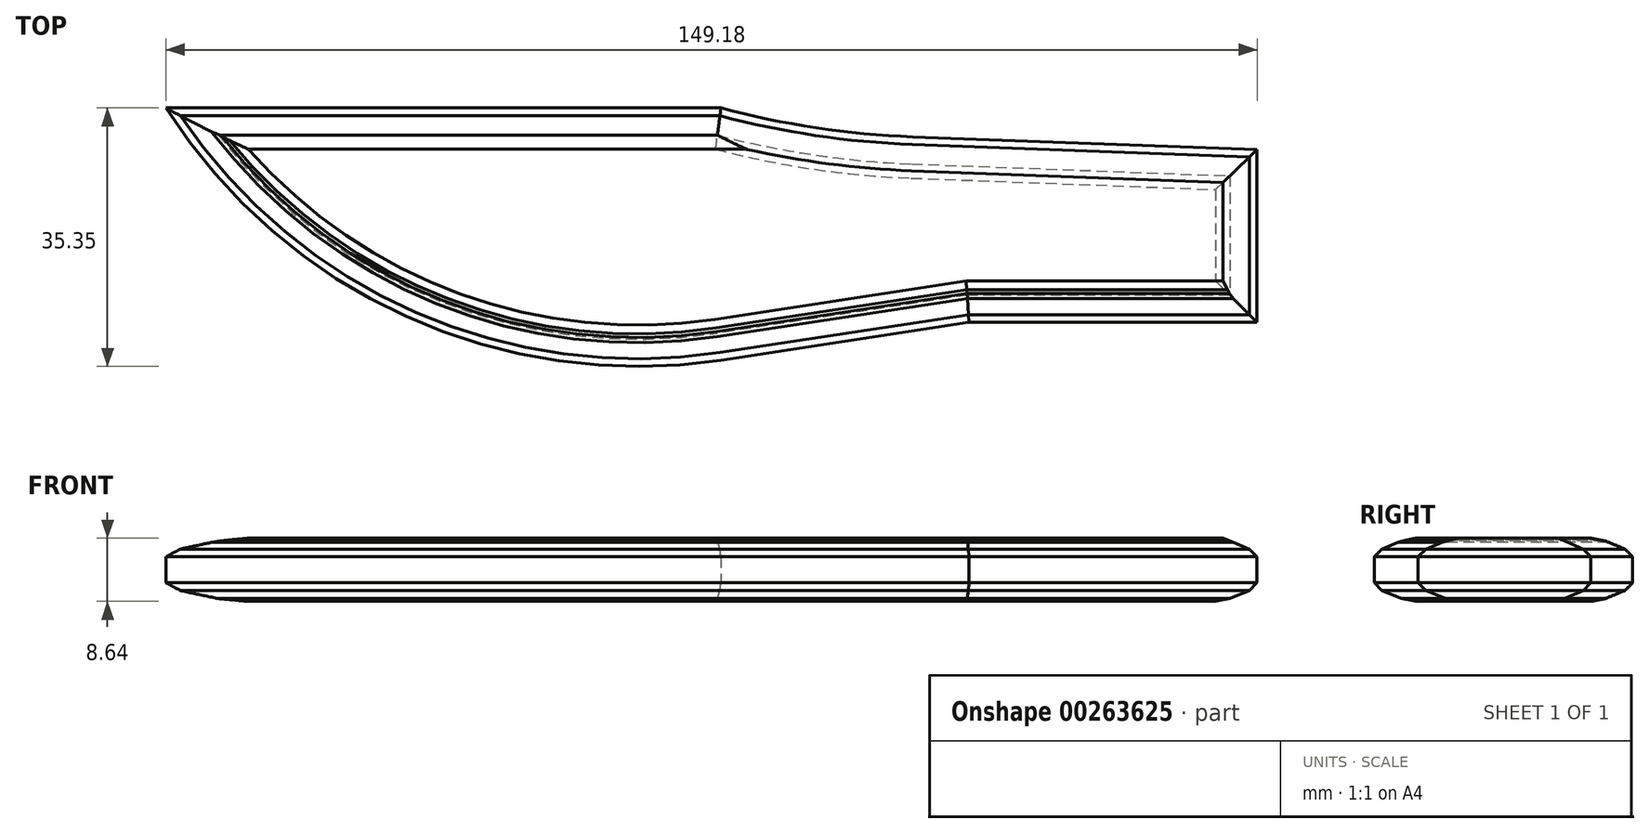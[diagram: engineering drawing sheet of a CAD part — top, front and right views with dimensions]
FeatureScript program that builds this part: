
annotation { "Feature Type Name" : "Feature", "Feature Type Description" : "" }
export const myFeature = defineFeature(function(context is Context, id is Id, definition is map)
    precondition{}
    {
        {
            var Q0;
            Q0=qCreatedBy(makeId("Top.planeOp"),FACE);
            var sketch = newSketch(context, id + "F0", { "sketchPlane" : qUnion([Q0])});
            skLineSegment(sketch, "E0", {"start": v(-62.27, 14.58) * mm, "end": v(13.6, 14.58) * mm});
            skArc(sketch, "E1", {"start": v(-62.27, 14.58) * mm, "mid": v(-29.46, -13.93) * mm, "end": v(13.6, -19.9) * mm});
            skLineSegment(sketch, "E2", {"start": v(13.6, -19.9) * mm, "end": v(47.54, -14.74) * mm});
            skLineSegment(sketch, "E3", {"start": v(47.54, -14.74) * mm, "end": v(86.9, -14.74) * mm});
            skLineSegment(sketch, "E4", {"start": v(86.9, -14.74) * mm, "end": v(86.9, 8.87) * mm});
            skLineSegment(sketch, "E5", {"start": v(86.9, 8.87) * mm, "end": v(39.8, 10.64) * mm});
            skArc(sketch, "E6", {"start": v(13.6, 14.58) * mm, "mid": v(26.6, 11.88) * mm, "end": v(39.8, 10.64) * mm});
            skSolve(sketch);
        }
        {
            var Q0;
            Q0 = qSketchRegion(id + "F0", true);
            extrude(context, id + "F1", {"entities" : qUnion([Q0]), "depth" : 8.64 * mm});
        }
        {
            var Q0;
            Q0=makeQuery(id+"F1.opExtrude","CAP_FACE",FACE,{"disambiguationData":[OSD([sQuery(id+"F0.wireOp",EDGE,"E0"),sQuery(id+"F0.wireOp",EDGE,"E1"),sQuery(id+"F0.wireOp",EDGE,"E2"),sQuery(id+"F0.wireOp",EDGE,"E3"),sQuery(id+"F0.wireOp",EDGE,"E4"),sQuery(id+"F0.wireOp",EDGE,"E5"),sQuery(id+"F0.wireOp",EDGE,"E6")])],"isStart":true});
            var Q1;
            Q1=makeQuery(id+"F1.opExtrude","CAP_FACE",FACE,{"disambiguationData":[OSD([sQuery(id+"F0.wireOp",EDGE,"E0"),sQuery(id+"F0.wireOp",EDGE,"E1"),sQuery(id+"F0.wireOp",EDGE,"E2"),sQuery(id+"F0.wireOp",EDGE,"E3"),sQuery(id+"F0.wireOp",EDGE,"E4"),sQuery(id+"F0.wireOp",EDGE,"E5"),sQuery(id+"F0.wireOp",EDGE,"E6")])],"isStart":false});
            chamfer(context, id + "F2", {"entities" : qUnion([Q0, Q1]), "width" : 2.54 * mm, "tangentPropagation" : true});
        }
        {
            var Q0;
            Q0=makeQuery(id+"F1.opExtrude","CAP_FACE",FACE,{"disambiguationData":[OSD([sQuery(id+"F0.wireOp",EDGE,"E0"),sQuery(id+"F0.wireOp",EDGE,"E1"),sQuery(id+"F0.wireOp",EDGE,"E2"),sQuery(id+"F0.wireOp",EDGE,"E3"),sQuery(id+"F0.wireOp",EDGE,"E4"),sQuery(id+"F0.wireOp",EDGE,"E5"),sQuery(id+"F0.wireOp",EDGE,"E6")])],"isStart":true});
            var Q1;
            Q1=makeQuery(id+"F1.opExtrude","CAP_FACE",FACE,{"disambiguationData":[OSD([sQuery(id+"F0.wireOp",EDGE,"E0"),sQuery(id+"F0.wireOp",EDGE,"E1"),sQuery(id+"F0.wireOp",EDGE,"E2"),sQuery(id+"F0.wireOp",EDGE,"E3"),sQuery(id+"F0.wireOp",EDGE,"E4"),sQuery(id+"F0.wireOp",EDGE,"E5"),sQuery(id+"F0.wireOp",EDGE,"E6")])],"isStart":false});
            chamfer(context, id + "F3", {"entities" : qUnion([Q0, Q1]), "width" : 5.08 * mm, "tangentPropagation" : true});
        }
        {
            var Q0;
            Q0=makeQuery(id+"F1.opExtrude","CAP_FACE",FACE,{"disambiguationData":[OSD([sQuery(id+"F0.wireOp",EDGE,"E0"),sQuery(id+"F0.wireOp",EDGE,"E1"),sQuery(id+"F0.wireOp",EDGE,"E2"),sQuery(id+"F0.wireOp",EDGE,"E3"),sQuery(id+"F0.wireOp",EDGE,"E4"),sQuery(id+"F0.wireOp",EDGE,"E5"),sQuery(id+"F0.wireOp",EDGE,"E6")])],"isStart":true});
            chamfer(context, id + "F4", {"entities" : qUnion([Q0]), "width" : 5.08 * mm, "tangentPropagation" : true});
        }
        {
            var Q0;
            {var subQ0=sQuery(id+"F0.wireOp",EDGE,"E1");var subQ1=makeQuery(id+"F1.opExtrude","CAP_FACE",FACE,{"disambiguationData":[OSD([sQuery(id+"F0.wireOp",EDGE,"E0"),subQ0,sQuery(id+"F0.wireOp",EDGE,"E2"),sQuery(id+"F0.wireOp",EDGE,"E3"),sQuery(id+"F0.wireOp",EDGE,"E4"),sQuery(id+"F0.wireOp",EDGE,"E5"),sQuery(id+"F0.wireOp",EDGE,"E6")])],"isStart":true});Q0=makeQuery(id+"F3.opChamfer","BLEND_EDGE",EDGE,{"blendedFrom":[makeQuery(id+"F2.opChamfer","BLEND_EDGE",EDGE,{"blendedFrom":[makeQuery(id+"F1.opExtrude","CAP_EDGE",EDGE,{"disambiguationData":[OSD([subQ0])],"isStart":true}),subQ1],"blendedInto":[subQ1]}),subQ1],"blendedInto":[subQ1]});}
            var Q1;
            {var subQ0=sQuery(id+"F0.wireOp",EDGE,"E1");var subQ1=makeQuery(id+"F1.opExtrude","CAP_FACE",FACE,{"disambiguationData":[OSD([sQuery(id+"F0.wireOp",EDGE,"E0"),subQ0,sQuery(id+"F0.wireOp",EDGE,"E2"),sQuery(id+"F0.wireOp",EDGE,"E3"),sQuery(id+"F0.wireOp",EDGE,"E4"),sQuery(id+"F0.wireOp",EDGE,"E5"),sQuery(id+"F0.wireOp",EDGE,"E6")])],"isStart":false});Q1=makeQuery(id+"F3.opChamfer","BLEND_EDGE",EDGE,{"blendedFrom":[makeQuery(id+"F2.opChamfer","BLEND_EDGE",EDGE,{"blendedFrom":[makeQuery(id+"F1.opExtrude","CAP_EDGE",EDGE,{"disambiguationData":[OSD([subQ0])],"isStart":false}),subQ1],"blendedInto":[subQ1]}),subQ1],"blendedInto":[subQ1]});}
            var Q2;
            {var subQ0=sQuery(id+"F0.wireOp",EDGE,"E0");var subQ1=makeQuery(id+"F1.opExtrude","CAP_FACE",FACE,{"disambiguationData":[OSD([subQ0,sQuery(id+"F0.wireOp",EDGE,"E1"),sQuery(id+"F0.wireOp",EDGE,"E2"),sQuery(id+"F0.wireOp",EDGE,"E3"),sQuery(id+"F0.wireOp",EDGE,"E4"),sQuery(id+"F0.wireOp",EDGE,"E5"),sQuery(id+"F0.wireOp",EDGE,"E6")])],"isStart":true});Q2=makeQuery(id+"F3.opChamfer","BLEND_EDGE",EDGE,{"blendedFrom":[makeQuery(id+"F2.opChamfer","BLEND_EDGE",EDGE,{"blendedFrom":[makeQuery(id+"F1.opExtrude","CAP_EDGE",EDGE,{"disambiguationData":[OSD([subQ0])],"isStart":true}),subQ1],"blendedInto":[subQ1]}),subQ1],"blendedInto":[subQ1]});}
            var Q3;
            {var subQ0=sQuery(id+"F0.wireOp",EDGE,"E0");var subQ1=makeQuery(id+"F1.opExtrude","CAP_FACE",FACE,{"disambiguationData":[OSD([subQ0,sQuery(id+"F0.wireOp",EDGE,"E1"),sQuery(id+"F0.wireOp",EDGE,"E2"),sQuery(id+"F0.wireOp",EDGE,"E3"),sQuery(id+"F0.wireOp",EDGE,"E4"),sQuery(id+"F0.wireOp",EDGE,"E5"),sQuery(id+"F0.wireOp",EDGE,"E6")])],"isStart":false});Q3=makeQuery(id+"F3.opChamfer","BLEND_EDGE",EDGE,{"blendedFrom":[makeQuery(id+"F2.opChamfer","BLEND_EDGE",EDGE,{"blendedFrom":[makeQuery(id+"F1.opExtrude","CAP_EDGE",EDGE,{"disambiguationData":[OSD([subQ0])],"isStart":false}),subQ1],"blendedInto":[subQ1]}),subQ1],"blendedInto":[subQ1]});}
            chamfer(context, id + "F5", {"entities" : qUnion([Q0, Q1, Q2, Q3]), "width" : 5.08 * mm, "tangentPropagation" : true});
        }
        {
            var Q0;
            {var subQ0=sQuery(id+"F0.wireOp",EDGE,"E6");var subQ1=sQuery(id+"F0.wireOp",EDGE,"E5");var subQ2=sQuery(id+"F0.wireOp",EDGE,"E4");var subQ3=sQuery(id+"F0.wireOp",EDGE,"E3");var subQ4=sQuery(id+"F0.wireOp",EDGE,"E2");var subQ5=sQuery(id+"F0.wireOp",EDGE,"E1");var subQ6=sQuery(id+"F0.wireOp",EDGE,"E0");var subQ7=makeQuery(id+"F1.opExtrude","CAP_FACE",FACE,{"disambiguationData":[OSD([subQ6,subQ5,subQ4,subQ3,subQ2,subQ1,subQ0])],"isStart":true});var subQ8=makeQuery(id+"F2.opChamfer","BLEND_EDGE",EDGE,{"blendedFrom":[makeQuery(id+"F1.opExtrude","CAP_EDGE",EDGE,{"disambiguationData":[OSD([subQ5])],"isStart":true}),subQ7],"blendedInto":[subQ7]});Q0=makeQuery(id+"F5.opChamfer","BLEND_EDGE",EDGE,{"blendedFrom":[makeQuery(id+"F3.opChamfer","BLEND_EDGE",EDGE,{"blendedFrom":[subQ8,subQ7],"blendedInto":[subQ7]}),makeQuery(id+"F3.opChamfer","BLEND_FACE",FACE,{"disambiguationData":[OSD([subQ6,subQ5,subQ4,subQ3,subQ2,subQ1,subQ0]),TDD([subQ8])]})],"blendedInto":[makeQuery(id+"F3.opChamfer","BLEND_FACE",FACE,{"disambiguationData":[OSD([subQ6,subQ5,subQ4,subQ3,subQ2,subQ1,subQ0]),TDD([subQ8])]})]});}
            var Q1;
            {var subQ0=sQuery(id+"F0.wireOp",EDGE,"E6");var subQ1=sQuery(id+"F0.wireOp",EDGE,"E5");var subQ2=sQuery(id+"F0.wireOp",EDGE,"E4");var subQ3=sQuery(id+"F0.wireOp",EDGE,"E3");var subQ4=sQuery(id+"F0.wireOp",EDGE,"E2");var subQ5=sQuery(id+"F0.wireOp",EDGE,"E1");var subQ6=sQuery(id+"F0.wireOp",EDGE,"E0");var subQ7=makeQuery(id+"F1.opExtrude","CAP_FACE",FACE,{"disambiguationData":[OSD([subQ6,subQ5,subQ4,subQ3,subQ2,subQ1,subQ0])],"isStart":false});var subQ8=makeQuery(id+"F2.opChamfer","BLEND_EDGE",EDGE,{"blendedFrom":[makeQuery(id+"F1.opExtrude","CAP_EDGE",EDGE,{"disambiguationData":[OSD([subQ5])],"isStart":false}),subQ7],"blendedInto":[subQ7]});Q1=makeQuery(id+"F5.opChamfer","BLEND_EDGE",EDGE,{"blendedFrom":[makeQuery(id+"F3.opChamfer","BLEND_EDGE",EDGE,{"blendedFrom":[subQ8,subQ7],"blendedInto":[subQ7]}),makeQuery(id+"F3.opChamfer","BLEND_FACE",FACE,{"disambiguationData":[OSD([subQ6,subQ5,subQ4,subQ3,subQ2,subQ1,subQ0]),TDD([subQ8])]})],"blendedInto":[makeQuery(id+"F3.opChamfer","BLEND_FACE",FACE,{"disambiguationData":[OSD([subQ6,subQ5,subQ4,subQ3,subQ2,subQ1,subQ0]),TDD([subQ8])]})]});}
            chamfer(context, id + "F6", {"entities" : qUnion([Q0, Q1]), "width" : 5.08 * mm, "tangentPropagation" : true});
        }
        {
            var Q0;
            {var subQ0=sQuery(id+"F0.wireOp",EDGE,"E6");var subQ1=sQuery(id+"F0.wireOp",EDGE,"E5");var subQ2=sQuery(id+"F0.wireOp",EDGE,"E4");var subQ3=sQuery(id+"F0.wireOp",EDGE,"E3");var subQ4=sQuery(id+"F0.wireOp",EDGE,"E2");var subQ5=sQuery(id+"F0.wireOp",EDGE,"E1");var subQ6=sQuery(id+"F0.wireOp",EDGE,"E0");var subQ7=makeQuery(id+"F1.opExtrude","CAP_FACE",FACE,{"disambiguationData":[OSD([subQ6,subQ5,subQ4,subQ3,subQ2,subQ1,subQ0])],"isStart":true});var subQ8=makeQuery(id+"F2.opChamfer","BLEND_EDGE",EDGE,{"blendedFrom":[makeQuery(id+"F1.opExtrude","CAP_EDGE",EDGE,{"disambiguationData":[OSD([subQ4])],"isStart":true}),subQ7],"blendedInto":[subQ7]});var subQ9=makeQuery(id+"F3.opChamfer","BLEND_EDGE",EDGE,{"blendedFrom":[subQ8,subQ7],"blendedInto":[subQ7]});Q0=makeQuery(id+"F6.opChamfer","BLEND_EDGE",EDGE,{"blendedFrom":[makeQuery(id+"F5.opChamfer","BLEND_EDGE",EDGE,{"blendedFrom":[subQ9,makeQuery(id+"F3.opChamfer","BLEND_FACE",FACE,{"disambiguationData":[OSD([subQ6,subQ5,subQ4,subQ3,subQ2,subQ1,subQ0]),TDD([subQ8])]})],"blendedInto":[makeQuery(id+"F3.opChamfer","BLEND_FACE",FACE,{"disambiguationData":[OSD([subQ6,subQ5,subQ4,subQ3,subQ2,subQ1,subQ0]),TDD([subQ8])]})]}),makeQuery(id+"F5.opChamfer","BLEND_FACE",FACE,{"disambiguationData":[OSD([subQ6,subQ5,subQ4,subQ3,subQ2,subQ1,subQ0]),TDD([subQ9])]})],"blendedInto":[makeQuery(id+"F5.opChamfer","BLEND_FACE",FACE,{"disambiguationData":[OSD([subQ6,subQ5,subQ4,subQ3,subQ2,subQ1,subQ0]),TDD([subQ9])]})]});}
            var Q1;
            {var subQ0=sQuery(id+"F0.wireOp",EDGE,"E6");var subQ1=sQuery(id+"F0.wireOp",EDGE,"E5");var subQ2=sQuery(id+"F0.wireOp",EDGE,"E4");var subQ3=sQuery(id+"F0.wireOp",EDGE,"E3");var subQ4=sQuery(id+"F0.wireOp",EDGE,"E2");var subQ5=sQuery(id+"F0.wireOp",EDGE,"E1");var subQ6=sQuery(id+"F0.wireOp",EDGE,"E0");var subQ7=makeQuery(id+"F1.opExtrude","CAP_FACE",FACE,{"disambiguationData":[OSD([subQ6,subQ5,subQ4,subQ3,subQ2,subQ1,subQ0])],"isStart":false});var subQ8=makeQuery(id+"F2.opChamfer","BLEND_EDGE",EDGE,{"blendedFrom":[makeQuery(id+"F1.opExtrude","CAP_EDGE",EDGE,{"disambiguationData":[OSD([subQ4])],"isStart":false}),subQ7],"blendedInto":[subQ7]});var subQ9=makeQuery(id+"F3.opChamfer","BLEND_EDGE",EDGE,{"blendedFrom":[subQ8,subQ7],"blendedInto":[subQ7]});Q1=makeQuery(id+"F6.opChamfer","BLEND_EDGE",EDGE,{"blendedFrom":[makeQuery(id+"F5.opChamfer","BLEND_EDGE",EDGE,{"blendedFrom":[subQ9,makeQuery(id+"F3.opChamfer","BLEND_FACE",FACE,{"disambiguationData":[OSD([subQ6,subQ5,subQ4,subQ3,subQ2,subQ1,subQ0]),TDD([subQ8])]})],"blendedInto":[makeQuery(id+"F3.opChamfer","BLEND_FACE",FACE,{"disambiguationData":[OSD([subQ6,subQ5,subQ4,subQ3,subQ2,subQ1,subQ0]),TDD([subQ8])]})]}),makeQuery(id+"F5.opChamfer","BLEND_FACE",FACE,{"disambiguationData":[OSD([subQ6,subQ5,subQ4,subQ3,subQ2,subQ1,subQ0]),TDD([subQ9])]})],"blendedInto":[makeQuery(id+"F5.opChamfer","BLEND_FACE",FACE,{"disambiguationData":[OSD([subQ6,subQ5,subQ4,subQ3,subQ2,subQ1,subQ0]),TDD([subQ9])]})]});}
            chamfer(context, id + "F7", {"entities" : qUnion([Q0, Q1]), "width" : 5.08 * mm, "tangentPropagation" : true});
        }
        {
            var Q0;
            {var subQ0=sQuery(id+"F0.wireOp",EDGE,"E3");var subQ1=makeQuery(id+"F1.opExtrude","CAP_FACE",FACE,{"disambiguationData":[OSD([sQuery(id+"F0.wireOp",EDGE,"E0"),sQuery(id+"F0.wireOp",EDGE,"E1"),sQuery(id+"F0.wireOp",EDGE,"E2"),subQ0,sQuery(id+"F0.wireOp",EDGE,"E4"),sQuery(id+"F0.wireOp",EDGE,"E5"),sQuery(id+"F0.wireOp",EDGE,"E6")])],"isStart":true});Q0=makeQuery(id+"F3.opChamfer","BLEND_EDGE",EDGE,{"blendedFrom":[makeQuery(id+"F2.opChamfer","BLEND_EDGE",EDGE,{"blendedFrom":[makeQuery(id+"F1.opExtrude","CAP_EDGE",EDGE,{"disambiguationData":[OSD([subQ0])],"isStart":true}),subQ1],"blendedInto":[subQ1]}),subQ1],"blendedInto":[subQ1]});}
            var Q1;
            {var subQ0=sQuery(id+"F0.wireOp",EDGE,"E3");var subQ1=makeQuery(id+"F1.opExtrude","CAP_FACE",FACE,{"disambiguationData":[OSD([sQuery(id+"F0.wireOp",EDGE,"E0"),sQuery(id+"F0.wireOp",EDGE,"E1"),sQuery(id+"F0.wireOp",EDGE,"E2"),subQ0,sQuery(id+"F0.wireOp",EDGE,"E4"),sQuery(id+"F0.wireOp",EDGE,"E5"),sQuery(id+"F0.wireOp",EDGE,"E6")])],"isStart":false});Q1=makeQuery(id+"F3.opChamfer","BLEND_EDGE",EDGE,{"blendedFrom":[makeQuery(id+"F2.opChamfer","BLEND_EDGE",EDGE,{"blendedFrom":[makeQuery(id+"F1.opExtrude","CAP_EDGE",EDGE,{"disambiguationData":[OSD([subQ0])],"isStart":false}),subQ1],"blendedInto":[subQ1]}),subQ1],"blendedInto":[subQ1]});}
            chamfer(context, id + "F8", {"entities" : qUnion([Q0, Q1]), "width" : 5.08 * mm, "tangentPropagation" : true});
        }
        {
            var Q0;
            {var subQ0=sQuery(id+"F0.wireOp",EDGE,"E6");var subQ1=sQuery(id+"F0.wireOp",EDGE,"E5");var subQ2=sQuery(id+"F0.wireOp",EDGE,"E4");var subQ3=sQuery(id+"F0.wireOp",EDGE,"E3");var subQ4=sQuery(id+"F0.wireOp",EDGE,"E2");var subQ5=sQuery(id+"F0.wireOp",EDGE,"E1");var subQ6=sQuery(id+"F0.wireOp",EDGE,"E0");var subQ7=makeQuery(id+"F1.opExtrude","CAP_FACE",FACE,{"disambiguationData":[OSD([subQ6,subQ5,subQ4,subQ3,subQ2,subQ1,subQ0])],"isStart":false});var subQ8=makeQuery(id+"F2.opChamfer","BLEND_EDGE",EDGE,{"blendedFrom":[makeQuery(id+"F1.opExtrude","CAP_EDGE",EDGE,{"disambiguationData":[OSD([subQ3])],"isStart":false}),subQ7],"blendedInto":[subQ7]});Q0=makeQuery(id+"F8.opChamfer","BLEND_EDGE",EDGE,{"blendedFrom":[makeQuery(id+"F3.opChamfer","BLEND_EDGE",EDGE,{"blendedFrom":[subQ8,subQ7],"blendedInto":[subQ7]}),makeQuery(id+"F3.opChamfer","BLEND_FACE",FACE,{"disambiguationData":[OSD([subQ6,subQ5,subQ4,subQ3,subQ2,subQ1,subQ0]),TDD([subQ8])]})],"blendedInto":[makeQuery(id+"F3.opChamfer","BLEND_FACE",FACE,{"disambiguationData":[OSD([subQ6,subQ5,subQ4,subQ3,subQ2,subQ1,subQ0]),TDD([subQ8])]})]});}
            var Q1;
            {var subQ0=sQuery(id+"F0.wireOp",EDGE,"E6");var subQ1=sQuery(id+"F0.wireOp",EDGE,"E5");var subQ2=sQuery(id+"F0.wireOp",EDGE,"E4");var subQ3=sQuery(id+"F0.wireOp",EDGE,"E3");var subQ4=sQuery(id+"F0.wireOp",EDGE,"E2");var subQ5=sQuery(id+"F0.wireOp",EDGE,"E1");var subQ6=sQuery(id+"F0.wireOp",EDGE,"E0");var subQ7=makeQuery(id+"F1.opExtrude","CAP_FACE",FACE,{"disambiguationData":[OSD([subQ6,subQ5,subQ4,subQ3,subQ2,subQ1,subQ0])],"isStart":true});var subQ8=makeQuery(id+"F2.opChamfer","BLEND_EDGE",EDGE,{"blendedFrom":[makeQuery(id+"F1.opExtrude","CAP_EDGE",EDGE,{"disambiguationData":[OSD([subQ3])],"isStart":true}),subQ7],"blendedInto":[subQ7]});Q1=makeQuery(id+"F8.opChamfer","BLEND_EDGE",EDGE,{"blendedFrom":[makeQuery(id+"F3.opChamfer","BLEND_EDGE",EDGE,{"blendedFrom":[subQ8,subQ7],"blendedInto":[subQ7]}),makeQuery(id+"F3.opChamfer","BLEND_FACE",FACE,{"disambiguationData":[OSD([subQ6,subQ5,subQ4,subQ3,subQ2,subQ1,subQ0]),TDD([subQ8])]})],"blendedInto":[makeQuery(id+"F3.opChamfer","BLEND_FACE",FACE,{"disambiguationData":[OSD([subQ6,subQ5,subQ4,subQ3,subQ2,subQ1,subQ0]),TDD([subQ8])]})]});}
            chamfer(context, id + "F9", {"entities" : qUnion([Q0, Q1]), "width" : 5.08 * mm, "tangentPropagation" : true});
        }
        {
            var Q0;
            {var subQ0=sQuery(id+"F0.wireOp",EDGE,"E6");var subQ1=sQuery(id+"F0.wireOp",EDGE,"E5");var subQ2=sQuery(id+"F0.wireOp",EDGE,"E4");var subQ3=sQuery(id+"F0.wireOp",EDGE,"E3");var subQ4=sQuery(id+"F0.wireOp",EDGE,"E2");var subQ5=sQuery(id+"F0.wireOp",EDGE,"E1");var subQ6=sQuery(id+"F0.wireOp",EDGE,"E0");var subQ7=makeQuery(id+"F1.opExtrude","CAP_FACE",FACE,{"disambiguationData":[OSD([subQ6,subQ5,subQ4,subQ3,subQ2,subQ1,subQ0])],"isStart":false});var subQ8=makeQuery(id+"F2.opChamfer","BLEND_EDGE",EDGE,{"blendedFrom":[makeQuery(id+"F1.opExtrude","CAP_EDGE",EDGE,{"disambiguationData":[OSD([subQ3])],"isStart":false}),subQ7],"blendedInto":[subQ7]});var subQ9=makeQuery(id+"F3.opChamfer","BLEND_EDGE",EDGE,{"blendedFrom":[subQ8,subQ7],"blendedInto":[subQ7]});Q0=makeQuery(id+"F9.opChamfer","BLEND_EDGE",EDGE,{"blendedFrom":[makeQuery(id+"F8.opChamfer","BLEND_EDGE",EDGE,{"blendedFrom":[subQ9,makeQuery(id+"F3.opChamfer","BLEND_FACE",FACE,{"disambiguationData":[OSD([subQ6,subQ5,subQ4,subQ3,subQ2,subQ1,subQ0]),TDD([subQ8])]})],"blendedInto":[makeQuery(id+"F3.opChamfer","BLEND_FACE",FACE,{"disambiguationData":[OSD([subQ6,subQ5,subQ4,subQ3,subQ2,subQ1,subQ0]),TDD([subQ8])]})]}),makeQuery(id+"F8.opChamfer","BLEND_FACE",FACE,{"disambiguationData":[OSD([subQ6,subQ5,subQ4,subQ3,subQ2,subQ1,subQ0]),TDD([subQ9])]})],"blendedInto":[makeQuery(id+"F8.opChamfer","BLEND_FACE",FACE,{"disambiguationData":[OSD([subQ6,subQ5,subQ4,subQ3,subQ2,subQ1,subQ0]),TDD([subQ9])]})]});}
            var Q1;
            {var subQ0=sQuery(id+"F0.wireOp",EDGE,"E6");var subQ1=sQuery(id+"F0.wireOp",EDGE,"E5");var subQ2=sQuery(id+"F0.wireOp",EDGE,"E4");var subQ3=sQuery(id+"F0.wireOp",EDGE,"E3");var subQ4=sQuery(id+"F0.wireOp",EDGE,"E2");var subQ5=sQuery(id+"F0.wireOp",EDGE,"E1");var subQ6=sQuery(id+"F0.wireOp",EDGE,"E0");var subQ7=makeQuery(id+"F1.opExtrude","CAP_FACE",FACE,{"disambiguationData":[OSD([subQ6,subQ5,subQ4,subQ3,subQ2,subQ1,subQ0])],"isStart":true});var subQ8=makeQuery(id+"F2.opChamfer","BLEND_EDGE",EDGE,{"blendedFrom":[makeQuery(id+"F1.opExtrude","CAP_EDGE",EDGE,{"disambiguationData":[OSD([subQ3])],"isStart":true}),subQ7],"blendedInto":[subQ7]});var subQ9=makeQuery(id+"F3.opChamfer","BLEND_EDGE",EDGE,{"blendedFrom":[subQ8,subQ7],"blendedInto":[subQ7]});Q1=makeQuery(id+"F9.opChamfer","BLEND_EDGE",EDGE,{"blendedFrom":[makeQuery(id+"F8.opChamfer","BLEND_EDGE",EDGE,{"blendedFrom":[subQ9,makeQuery(id+"F3.opChamfer","BLEND_FACE",FACE,{"disambiguationData":[OSD([subQ6,subQ5,subQ4,subQ3,subQ2,subQ1,subQ0]),TDD([subQ8])]})],"blendedInto":[makeQuery(id+"F3.opChamfer","BLEND_FACE",FACE,{"disambiguationData":[OSD([subQ6,subQ5,subQ4,subQ3,subQ2,subQ1,subQ0]),TDD([subQ8])]})]}),makeQuery(id+"F8.opChamfer","BLEND_FACE",FACE,{"disambiguationData":[OSD([subQ6,subQ5,subQ4,subQ3,subQ2,subQ1,subQ0]),TDD([subQ9])]})],"blendedInto":[makeQuery(id+"F8.opChamfer","BLEND_FACE",FACE,{"disambiguationData":[OSD([subQ6,subQ5,subQ4,subQ3,subQ2,subQ1,subQ0]),TDD([subQ9])]})]});}
            chamfer(context, id + "F10", {"entities" : qUnion([Q0, Q1]), "width" : 5.08 * mm, "tangentPropagation" : true});
        }
    });
